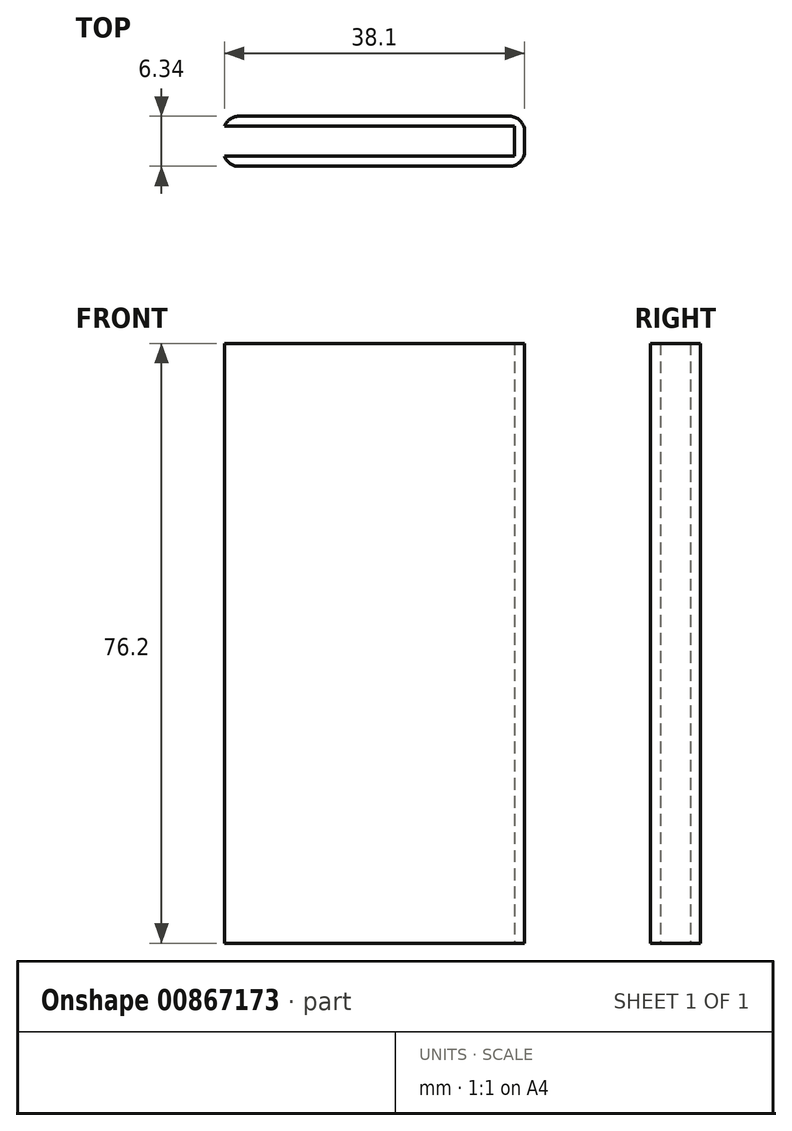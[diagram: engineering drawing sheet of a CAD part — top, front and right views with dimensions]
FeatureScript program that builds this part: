
annotation { "Feature Type Name" : "Feature", "Feature Type Description" : "" }
export const myFeature = defineFeature(function(context is Context, id is Id, definition is map)
    precondition{}
    {
        {
            var Q0;
            Q0=qCreatedBy(makeId("Top.planeOp"),FACE);
            var sketch = newSketch(context, id + "F0", { "sketchPlane" : qUnion([Q0])});
            skLineSegment(sketch, "E0.bottom", {"start": v(19.05, -3.18) * mm, "end": v(-19.05, -3.18) * mm});
            skLineSegment(sketch, "E0.top", {"start": v(19.05, 3.18) * mm, "end": v(-19.05, 3.18) * mm});
            skLineSegment(sketch, "E0.left", {"start": v(19.05, -3.18) * mm, "end": v(19.05, 3.17) * mm});
            skLineSegment(sketch, "E0.right", {"start": v(-19.05, -3.18) * mm, "end": v(-19.05, -1.9) * mm});
            skPoint(sketch, "E0.middle", {"position": v(0, 0) * mm});
            skLineSegment(sketch, "E1.left", {"start": v(17.78, -1.9) * mm, "end": v(17.78, 1.9) * mm});
            skLineSegment(sketch, "E2.trimOffspring", {"start": v(-19.05, 1.9) * mm, "end": v(-19.05, 3.17) * mm});
            skLineSegment(sketch, "E3", {"start": v(-19.05, 1.9) * mm, "end": v(17.78, 1.9) * mm});
            skLineSegment(sketch, "E4", {"start": v(-19.05, -1.9) * mm, "end": v(17.78, -1.9) * mm});
            skSolve(sketch);
        }
        {
            var Q0;
            Q0 = qSketchRegion(id + "F0", true);
            extrude(context, id + "F1", {"entities" : qUnion([Q0]), "depth" : 76.2 * mm, "offsetDistance" : 25.4 * mm});
        }
        {
            var Q0;
            Q0=makeQuery(id+"F1.opExtrude","SWEPT_EDGE",EDGE,{"disambiguationData":[OSD([sQuery(id+"F0.wireOp",EDGE,"E0.top"),sQuery(id+"F0.wireOp",EDGE,"E0.left")])]});
            var Q1;
            Q1=makeQuery(id+"F1.opExtrude","SWEPT_EDGE",EDGE,{"disambiguationData":[OSD([sQuery(id+"F0.wireOp",EDGE,"E0.bottom"),sQuery(id+"F0.wireOp",EDGE,"E0.left")])]});
            var Q2;
            Q2=makeQuery(id+"F1.opExtrude","SWEPT_EDGE",EDGE,{"disambiguationData":[OSD([sQuery(id+"F0.wireOp",EDGE,"E0.bottom"),sQuery(id+"F0.wireOp",EDGE,"E0.right")])]});
            var Q3;
            Q3=makeQuery(id+"F1.opExtrude","SWEPT_EDGE",EDGE,{"disambiguationData":[OSD([sQuery(id+"F0.wireOp",EDGE,"E0.top"),sQuery(id+"F0.wireOp",EDGE,"E2.trimOffspring")])]});
            fillet(context, id + "F2", {"entities" : qUnion([Q0, Q1, Q2, Q3]), "radius" : 1.9 * mm, "tangentPropagation" : true, "allowEdgeOverflow" : false});
        }
    });
